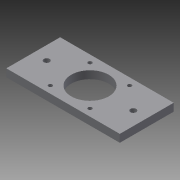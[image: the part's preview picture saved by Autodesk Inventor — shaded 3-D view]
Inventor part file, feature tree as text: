
AUTODESK INVENTOR PART (.ipt)
format: ipt  version: 2015 SP1 (Build 190203100, 203)  size: 97,792 bytes
history: native  units: mm
features: hole x2, extrude x1, sketch x1
ambient origin geometry x8: Origin, YZ Plane, XZ Plane, XY Plane, X Axis, Y Axis, Z Axis, Center Point
bodies: Body1 (feature_tree)
feature tree (4):
  extrude  "Extrusion2"  Depth=8.0mm
  hole  "Hole1"  [1 undecoded]
  hole  "Hole2"  [1 undecoded]
  sketch  "Sketch1"  dims[d4=39.0mm d5=28.0mm d6=59.0mm d7=4.0mm d8=38.415mm d9=40.0mm d11=360.0deg d13=7.415mm d14=8.0mm d15=0.0mm d16=104.0mm d17=28.0mm d18=6.0mm d19=6.0mm d20=4.0mm d21=2.0mm d22=90.0deg d23=8.0mm d24=20.594885mm d25=14.0mm d26=28.0mm d27=6.0mm d28=6.0mm d29=4.0mm d30=2.0mm d31=90.0deg d32=8.0mm d33=20.594885mm]
note: 2 required parameter values undecoded (feature->parameter linkage not recoverable at this tier; creation-order binding heuristic only, values carry confidence <= 0.55)
